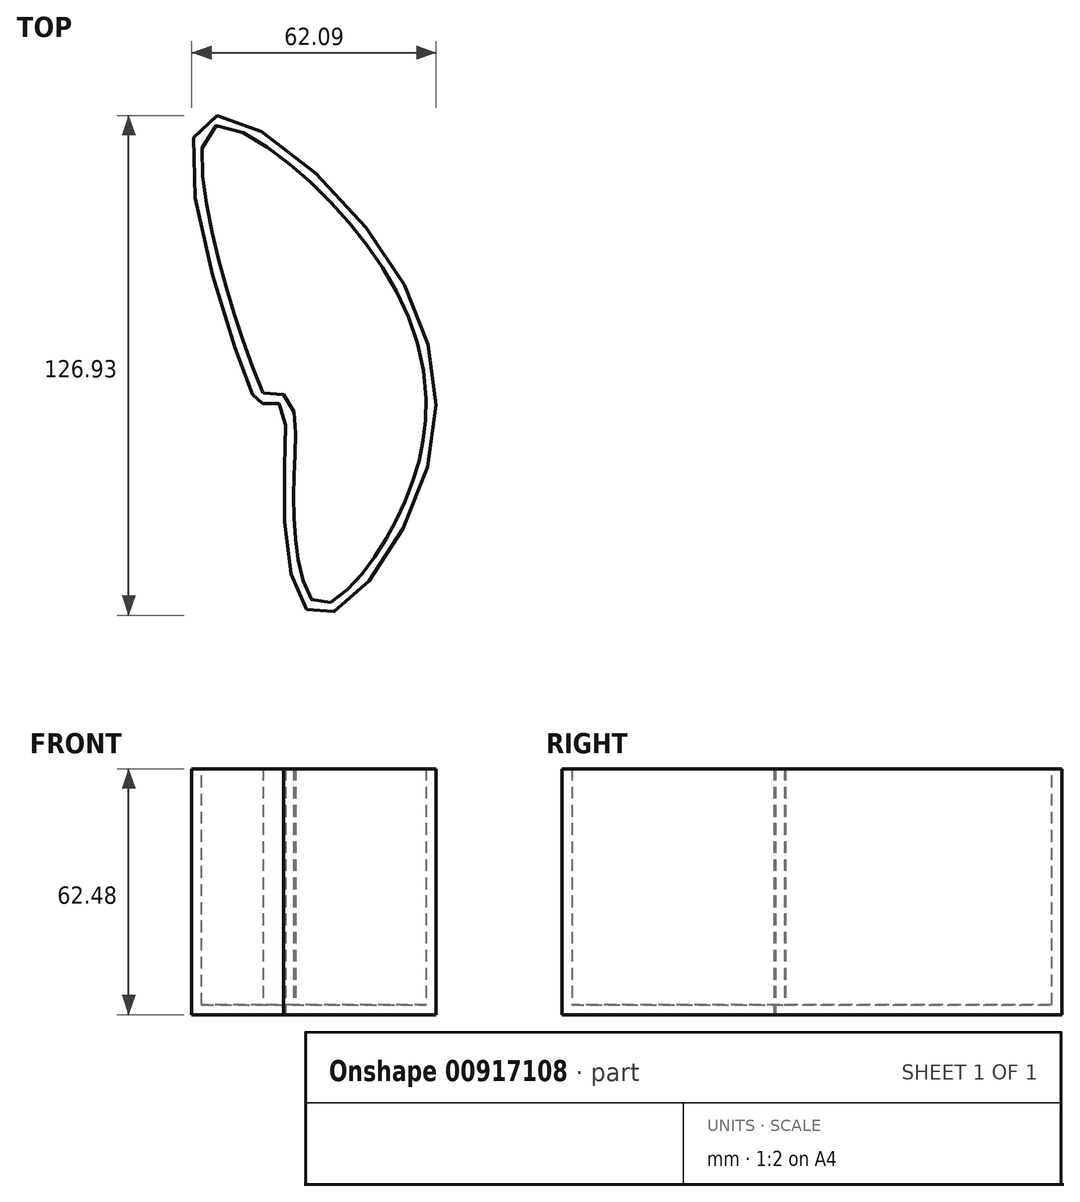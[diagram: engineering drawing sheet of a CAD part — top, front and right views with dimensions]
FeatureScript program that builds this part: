
annotation { "Feature Type Name" : "Feature", "Feature Type Description" : "" }
export const myFeature = defineFeature(function(context is Context, id is Id, definition is map)
    precondition{}
    {
        {
            var Q0;
            Q0=qCreatedBy(makeId("Top.planeOp"),FACE);
            var sketch = newSketch(context, id + "F0", { "sketchPlane" : qUnion([Q0])});
            skFitSpline(sketch, "E0", {"points": [v(-2.27, 2.23) * mm, v(-16.13, 70.5) * mm, v(25.62, 45.85) * mm, v(41.66, -18.02) * mm, v(13.9, -53.7) * mm, v(5.61, -22.32) * mm, v(4.42, 0) * mm, v(0, 0) * mm, v(-2.27, 2.23) * mm]});
            skSolve(sketch);
        }
        {
            var Q0;
            Q0=makeQuery(id+"F0.imprint","IMPRINT",FACE,{"disambiguationData":[TD([[makeQuery(id+"F0.imprint","IMPRINT",EDGE,{"derivedFrom":sQuery(id+"F0.wireOp",EDGE,"E0")}),-1.0]])]});
            extrude(context, id + "F1", {"entities" : qUnion([Q0]), "depth" : 62.48 * mm, "offsetDistance" : 25.4 * mm});
        }
        {
            var Q0;
            Q0=makeQuery(id+"F1.opExtrude","CAP_FACE",FACE,{"disambiguationData":[OSD([sQuery(id+"F0.wireOp",EDGE,"E0")])],"isStart":false});
            shell(context, id + "F2", {"entities" : qUnion([Q0]), "thickness" : 2.54 * mm});
        }
    });
